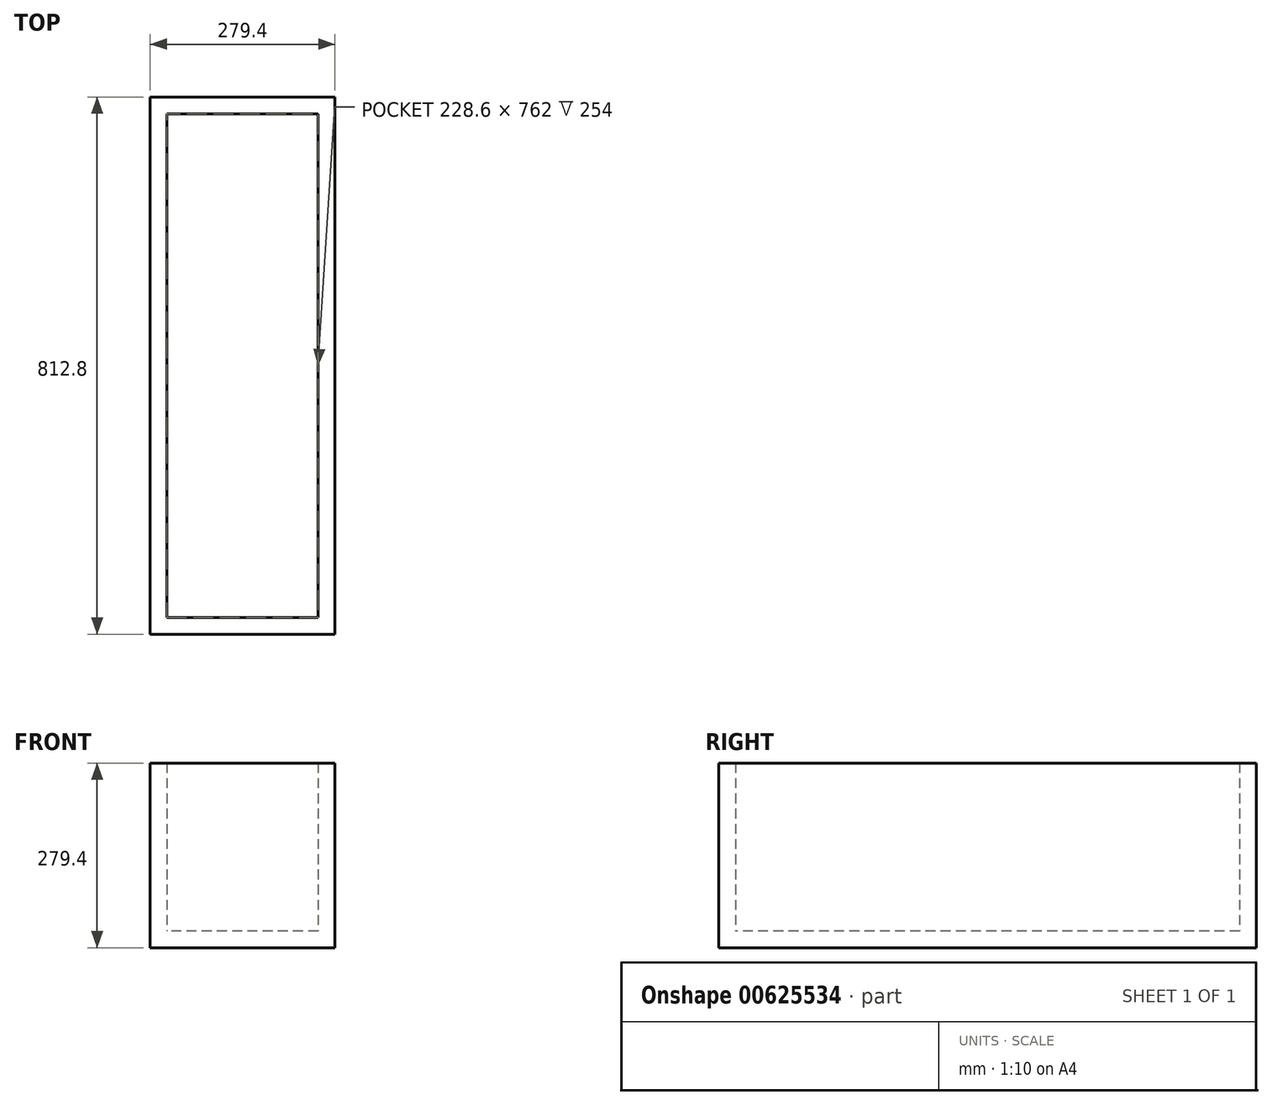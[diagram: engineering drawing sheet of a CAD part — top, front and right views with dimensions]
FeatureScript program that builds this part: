
annotation { "Feature Type Name" : "Feature", "Feature Type Description" : "" }
export const myFeature = defineFeature(function(context is Context, id is Id, definition is map)
    precondition{}
    {
        {
            var Q0;
            Q0=qCreatedBy(makeId("Top.planeOp"),FACE);
            var sketch = newSketch(context, id + "F0", { "sketchPlane" : qUnion([Q0])});
            skLineSegment(sketch, "E0.bottom", {"start": v(139.7, 406.4) * mm, "end": v(-139.7, 406.4) * mm});
            skLineSegment(sketch, "E0.top", {"start": v(139.7, -406.4) * mm, "end": v(-139.7, -406.4) * mm});
            skLineSegment(sketch, "E0.left", {"start": v(139.7, 406.4) * mm, "end": v(139.7, -406.4) * mm});
            skLineSegment(sketch, "E0.right", {"start": v(-139.7, 406.4) * mm, "end": v(-139.7, -406.4) * mm});
            skPoint(sketch, "E0.middle", {"position": v(0, 0) * mm});
            skSolve(sketch);
        }
        {
            var Q0;
            Q0=makeQuery(id+"F0.imprint","IMPRINT",FACE,{"disambiguationData":[TD([[makeQuery(id+"F0.imprint","IMPRINT",EDGE,{"derivedFrom":sQuery(id+"F0.wireOp",EDGE,"E0.bottom")}),1.0]])]});
            extrude(context, id + "F1", {"entities" : qUnion([Q0]), "depth" : 25.4 * mm, "offsetDistance" : 25.4 * mm});
        }
        {
            var Q0;
            Q0=makeQuery(id+"F1.opExtrude","CAP_FACE",FACE,{"disambiguationData":[OSD([sQuery(id+"F0.wireOp",EDGE,"E0.bottom"),sQuery(id+"F0.wireOp",EDGE,"E0.top"),sQuery(id+"F0.wireOp",EDGE,"E0.left"),sQuery(id+"F0.wireOp",EDGE,"E0.right")])],"isStart":false});
            var sketch = newSketch(context, id + "F2", { "sketchPlane" : qUnion([Q0])});
            skLineSegment(sketch, "E1.0", {"start": v(114.3, -381) * mm, "end": v(-114.3, -381) * mm});
            skLineSegment(sketch, "E1.1", {"start": v(114.3, 381) * mm, "end": v(114.3, -381) * mm});
            skLineSegment(sketch, "E1.2", {"start": v(114.3, 381) * mm, "end": v(-114.3, 381) * mm});
            skLineSegment(sketch, "E1.3", {"start": v(-114.3, 381) * mm, "end": v(-114.3, -381) * mm});
            skSolve(sketch);
        }
        {
            var Q0;
            Q0=makeQuery(id+"F2.imprint","IMPRINT",FACE,{"disambiguationData":[TD([[makeQuery(id+"F2.imprint","IMPRINT",EDGE,{"derivedFrom":sQuery(id+"F2.wireOp",EDGE,"E1.0")}),1.0]])]});
            extrude(context, id + "F3", {"entities" : qUnion([Q0]), "operationType" : NewBodyOperationType.ADD, "depth" : 254 * mm, "offsetDistance" : 25.4 * mm});
        }
    });
